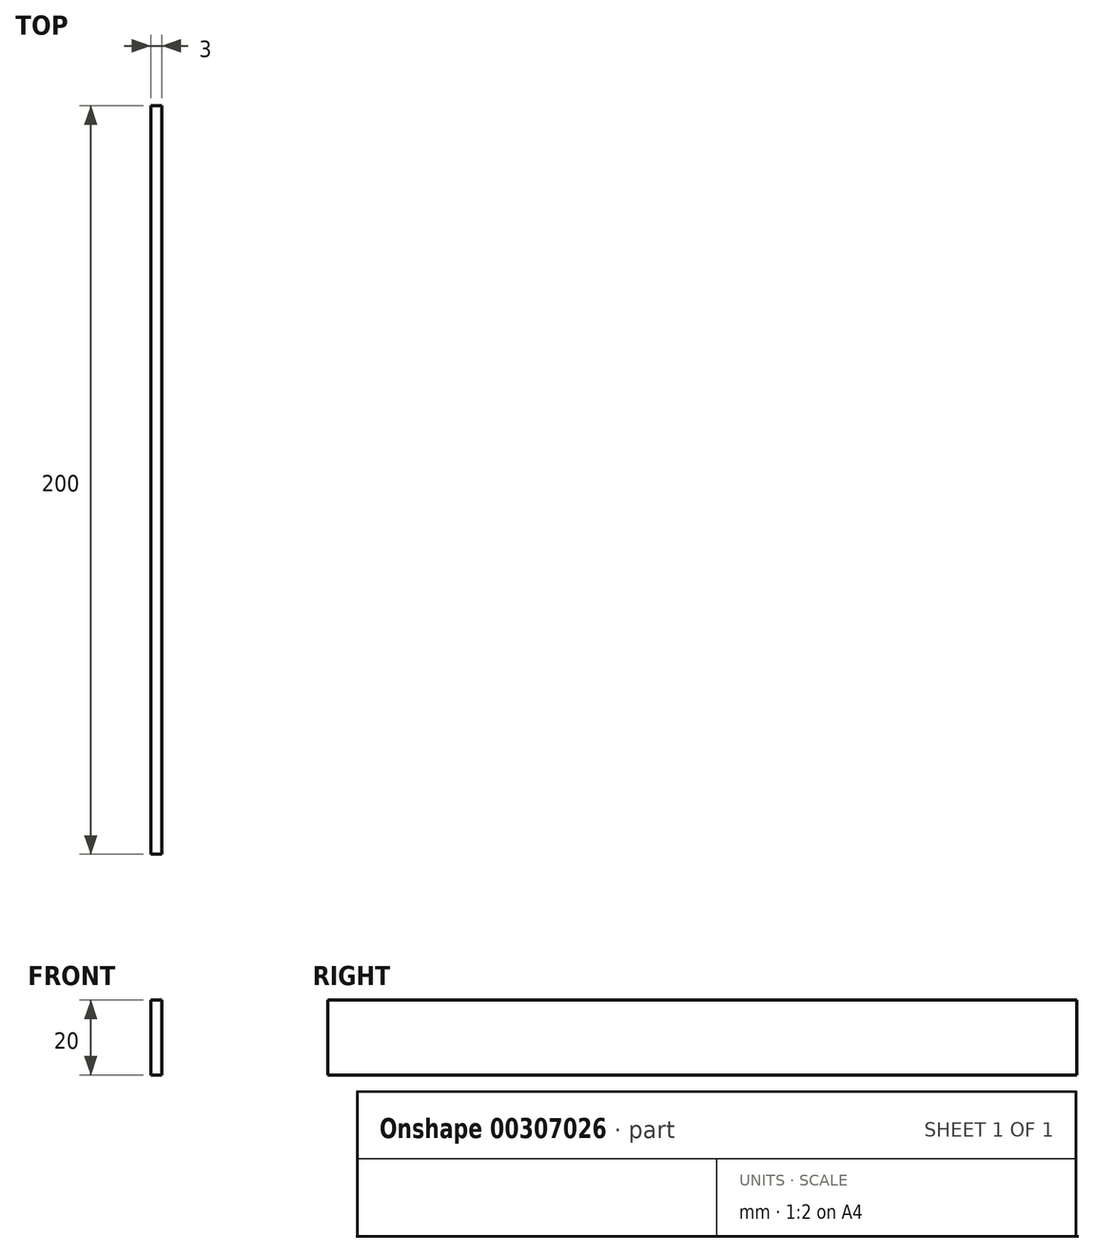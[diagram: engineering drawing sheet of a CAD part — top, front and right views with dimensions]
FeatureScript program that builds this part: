
annotation { "Feature Type Name" : "Feature", "Feature Type Description" : "" }
export const myFeature = defineFeature(function(context is Context, id is Id, definition is map)
    precondition{}
    {
        {
            var Q0;
            Q0=qCreatedBy(makeId("Front.planeOp"),FACE);
            var sketch = newSketch(context, id + "F0", { "sketchPlane" : qUnion([Q0])});
            skLineSegment(sketch, "E0.bottom", {"start": v(-0.2, 16.5) * mm, "end": v(2.8, 16.5) * mm});
            skLineSegment(sketch, "E0.top", {"start": v(-0.2, -3.5) * mm, "end": v(2.8, -3.5) * mm});
            skLineSegment(sketch, "E0.left", {"start": v(-0.2, 16.5) * mm, "end": v(-0.2, -3.5) * mm});
            skLineSegment(sketch, "E0.right", {"start": v(2.8, 16.5) * mm, "end": v(2.8, -3.5) * mm});
            skSolve(sketch);
        }
        {
            var Q0;
            Q0 = qSketchRegion(id + "F0", true);
            extrude(context, id + "F1", {"entities" : qUnion([Q0]), "depth" : 200 * mm});
        }
    });
